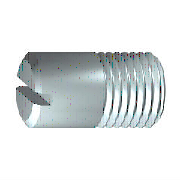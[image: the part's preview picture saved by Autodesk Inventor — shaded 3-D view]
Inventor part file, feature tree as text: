
AUTODESK INVENTOR PART (.ipt)
format: ipt  version: 2024 (Build 280153000, 153)  size: 161,792 bytes
history: native  units: mm (DEFAULTED — no unit token found)
features: other x2, extrude x1, plane x1
ambient origin geometry x8: Origin, YZ Plane, XZ Plane, XY Plane, X Axis, Y Axis, Z Axis, Center Point
bodies: Solid1 (feature_tree), Body (feature_tree)
feature tree (4):
  extrude  "Slot"  Depth=20.0mm
  other  "IDS_WORKPLANE"
  other  "Work Axis1"
  plane  "Work Plane2"
